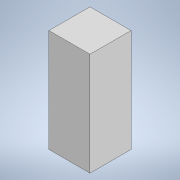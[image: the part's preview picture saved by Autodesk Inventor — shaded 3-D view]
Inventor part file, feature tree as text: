
AUTODESK INVENTOR PART (.ipt)
format: ipt  version: 2022 (Build 260153000, 153)  size: 89,088 bytes
history: native  units: mm
features: extrude x1, sketch x1
ambient origin geometry x8: Origin, YZ Plane, XZ Plane, XY Plane, X Axis, Y Axis, Z Axis, Center Point
bodies: Body1 (feature_tree)
feature tree (2):
  extrude  "Extrusion6"  Depth=30.0mm
  sketch  "Sketch8"  dims[d18=30.0mm d19=30.0mm d20=75.235mm d21=0.0mm]
